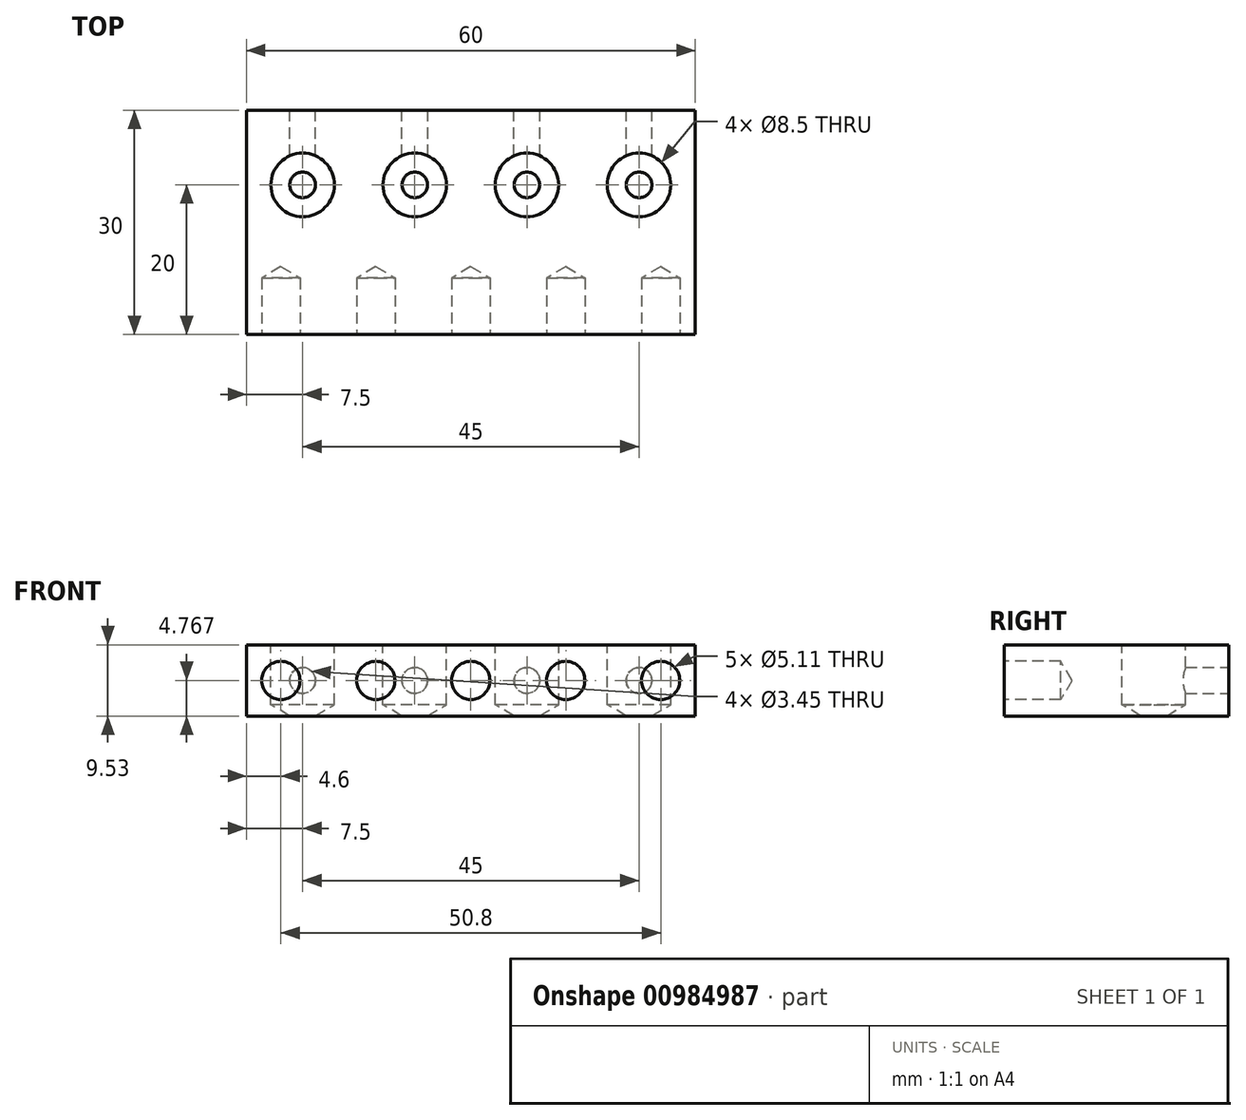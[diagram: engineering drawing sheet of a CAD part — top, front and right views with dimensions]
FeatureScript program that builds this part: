
annotation { "Feature Type Name" : "Feature", "Feature Type Description" : "" }
export const myFeature = defineFeature(function(context is Context, id is Id, definition is map)
    precondition{}
    {
        {
            var Q0;
            Q0=qCreatedBy(makeId("Top.planeOp"),FACE);
            var sketch = newSketch(context, id + "F0", { "sketchPlane" : qUnion([Q0])});
            skLineSegment(sketch, "E0.bottom", {"start": v(0, 0) * mm, "end": v(30, 0) * mm});
            skLineSegment(sketch, "E0.top", {"start": v(0, 30) * mm, "end": v(30, 30) * mm});
            skLineSegment(sketch, "E0.right", {"start": v(30, 0) * mm, "end": v(30, 30) * mm});
            skPoint(sketch, "E1", {"position": v(7.5, 20) * mm});
            skPoint(sketch, "E2.1.0.0", {"position": v(22.5, 20) * mm});
            skLineSegment(sketch, "E2.direction1", {"start": v(7.5, 20) * mm, "end": v(22.5, 20) * mm, "construction": true});
            skLineSegment(sketch, "E3.MirrorCS", {"start": v(0, 0) * mm, "end": v(-30, 0) * mm});
            skPoint(sketch, "E4.MirrorP", {"position": v(-22.5, 20) * mm});
            skLineSegment(sketch, "E5.MirrorCS", {"start": v(-7.5, 20) * mm, "end": v(-22.5, 20) * mm, "construction": true});
            skLineSegment(sketch, "E6.MirrorCS", {"start": v(0, 30) * mm, "end": v(-30, 30) * mm});
            skPoint(sketch, "E7.MirrorP", {"position": v(-7.5, 20) * mm});
            skLineSegment(sketch, "E8.MirrorCS", {"start": v(-30, 0) * mm, "end": v(-30, 30) * mm});
            skSolve(sketch);
        }
        {
            var Q0;
            Q0 = qSketchRegion(id + "F0", true);
            extrude(context, id + "F1", {"entities" : qUnion([Q0]), "oppositeDirection" : true, "depth" : 9.53 * mm, "offsetDistance" : 25 * mm});
        }
        {
            var Q0;
            Q0=sQuery(id+"F0.wireOp",VERTEX,"E4.MirrorP");
            var Q1;
            Q1=sQuery(id+"F0.wireOp",VERTEX,"E7.MirrorP");
            var Q2;
            Q2=sQuery(id+"F0.wireOp",VERTEX,"E1");
            var Q3;
            Q3=sQuery(id+"F0.wireOp",VERTEX,"E2.1.0.0");
            var Q4;
            Q4=makeQuery(id+"F1.opExtrude","SWEPT_BODY",BODY,{"disambiguationData":[OSD([sQuery(id+"F0.wireOp",EDGE,"E0.bottom"),sQuery(id+"F0.wireOp",EDGE,"E0.top"),sQuery(id+"F0.wireOp",EDGE,"E0.right"),sQuery(id+"F0.wireOp",EDGE,"E3.MirrorCS"),sQuery(id+"F0.wireOp",EDGE,"E6.MirrorCS"),sQuery(id+"F0.wireOp",EDGE,"E8.MirrorCS")])]});
            hole(context, id + "F2", {"style" : HoleStyle.SIMPLE, "endStyle" : HoleEndStyle.BLIND, "standardTappedOrClearance" : lookupTablePath({ "standard" : "ISO", "engagement" : "75%", "pitch" : "1.5 mm", "size" : "M10", "type" : "Tapped" }), "standardBlindInLast" : lookupTablePath({ "standard" : "ISO", "fit" : "Normal", "engagement" : "75%", "pitch" : "1.5 mm", "size" : "M10", "type" : "Clearance & tapped" }), "holeDiameter" : 8.5 * mm, "majorDiameter" : 10 * mm, "showTappedDepth" : true, "holeDepth" : 8 * mm, "isTappedThrough" : true, "tappedDepth" : 5 * mm, "tapClearance" : 2, "startFromSketch" : true, "locations" : qUnion([Q0, Q1, Q2, Q3]), "scope" : qUnion([Q4])});
        }
        {
            var Q0;
            Q0=makeQuery(id+"F1.opExtrude","SWEPT_FACE",FACE,{"disambiguationData":[OSD([sQuery(id+"F0.wireOp",EDGE,"E0.bottom"),sQuery(id+"F0.wireOp",EDGE,"E3.MirrorCS")])]});
            var sketch = newSketch(context, id + "F3", { "sketchPlane" : qUnion([Q0])});
            skPoint(sketch, "E9", {"position": v(0, -4.76) * mm});
            skPoint(sketch, "E9.positionSnap0", {"position": v(0, -9.53) * mm});
            skPoint(sketch, "E10.1.0.0", {"position": v(12.7, -4.76) * mm});
            skPoint(sketch, "E10.2.0.0", {"position": v(25.4, -4.76) * mm});
            skLineSegment(sketch, "E10.direction1", {"start": v(0, -4.76) * mm, "end": v(12.7, -4.76) * mm, "construction": true});
            skPoint(sketch, "E11.1.0.0", {"position": v(-12.7, -4.76) * mm});
            skPoint(sketch, "E11.2.0.0", {"position": v(-25.4, -4.76) * mm});
            skLineSegment(sketch, "E11.direction1", {"start": v(0, -4.76) * mm, "end": v(-12.7, -4.76) * mm, "construction": true});
            skSolve(sketch);
        }
        {
            var Q0;
            Q0=sQuery(id+"F3.wireOp",VERTEX,"E11.2.0.0");
            var Q1;
            Q1=sQuery(id+"F3.wireOp",VERTEX,"E11.1.0.0");
            var Q2;
            Q2=sQuery(id+"F3.wireOp",VERTEX,"E9");
            var Q3;
            Q3=sQuery(id+"F3.wireOp",VERTEX,"E10.1.0.0");
            var Q4;
            Q4=sQuery(id+"F3.wireOp",VERTEX,"E10.2.0.0");
            var Q5;
            Q5=makeQuery(id+"F1.opExtrude","SWEPT_BODY",BODY,{"disambiguationData":[OSD([sQuery(id+"F0.wireOp",EDGE,"E0.bottom"),sQuery(id+"F0.wireOp",EDGE,"E0.top"),sQuery(id+"F0.wireOp",EDGE,"E0.right"),sQuery(id+"F0.wireOp",EDGE,"E3.MirrorCS"),sQuery(id+"F0.wireOp",EDGE,"E6.MirrorCS"),sQuery(id+"F0.wireOp",EDGE,"E8.MirrorCS")])]});
            hole(context, id + "F4", {"style" : HoleStyle.SIMPLE, "endStyle" : HoleEndStyle.BLIND, "standardTappedOrClearance" : lookupTablePath({ "standard" : "ANSI", "engagement" : "75%", "pitch" : "20 tpi", "size" : "1/4", "type" : "Tapped" }), "standardBlindInLast" : lookupTablePath({ "standard" : "ANSI", "fit" : "Normal", "engagement" : "75%", "pitch" : "20 tpi", "size" : "1/4", "type" : "Clearance & tapped" }), "holeDiameter" : 5.1 * mm, "majorDiameter" : 6.35 * mm, "showTappedDepth" : true, "holeDepth" : 7.54 * mm, "isTappedThrough" : true, "tappedDepth" : 5 * mm, "tapClearance" : 2, "startFromSketch" : true, "locations" : qUnion([Q0, Q1, Q2, Q3, Q4]), "scope" : qUnion([Q5])});
        }
        {
            var Q0;
            Q0=makeQuery(id+"F1.opExtrude","SWEPT_FACE",FACE,{"disambiguationData":[OSD([sQuery(id+"F0.wireOp",EDGE,"E0.top"),sQuery(id+"F0.wireOp",EDGE,"E6.MirrorCS")])]});
            var sketch = newSketch(context, id + "F5", { "sketchPlane" : qUnion([Q0])});
            skPoint(sketch, "E12", {"position": v(-22.5, -4.76) * mm});
            skPoint(sketch, "E13.1.0.0", {"position": v(-7.5, -4.76) * mm});
            skPoint(sketch, "E13.2.0.0", {"position": v(7.5, -4.76) * mm});
            skPoint(sketch, "E13.3.0.0", {"position": v(22.5, -4.76) * mm});
            skLineSegment(sketch, "E13.direction1", {"start": v(-22.5, -4.76) * mm, "end": v(-7.5, -4.76) * mm, "construction": true});
            skSolve(sketch);
        }
        {
            var Q0;
            Q0=sQuery(id+"F5.wireOp",VERTEX,"E12");
            var Q1;
            Q1=sQuery(id+"F5.wireOp",VERTEX,"E13.1.0.0");
            var Q2;
            Q2=sQuery(id+"F5.wireOp",VERTEX,"E13.2.0.0");
            var Q3;
            Q3=sQuery(id+"F5.wireOp",VERTEX,"E13.3.0.0");
            var Q4;
            Q4=makeQuery(id+"F1.opExtrude","SWEPT_BODY",BODY,{"disambiguationData":[OSD([sQuery(id+"F0.wireOp",EDGE,"E0.bottom"),sQuery(id+"F0.wireOp",EDGE,"E0.top"),sQuery(id+"F0.wireOp",EDGE,"E0.right"),sQuery(id+"F0.wireOp",EDGE,"E3.MirrorCS"),sQuery(id+"F0.wireOp",EDGE,"E6.MirrorCS"),sQuery(id+"F0.wireOp",EDGE,"E8.MirrorCS")])]});
            hole(context, id + "F6", {"style" : HoleStyle.SIMPLE, "endStyle" : HoleEndStyle.BLIND, "standardTappedOrClearance" : lookupTablePath({ "standard" : "ANSI", "engagement" : "75%", "pitch" : "32 tpi", "size" : "#8", "type" : "Tapped" }), "standardBlindInLast" : lookupTablePath({ "standard" : "ANSI", "fit" : "Normal", "engagement" : "75%", "pitch" : "32 tpi", "size" : "#8", "type" : "Clearance & tapped" }), "holeDiameter" : 3.45 * mm, "majorDiameter" : 4.17 * mm, "showTappedDepth" : true, "holeDepth" : 6.6 * mm, "isTappedThrough" : true, "tappedDepth" : 5 * mm, "tapClearance" : 2, "startFromSketch" : true, "locations" : qUnion([Q0, Q1, Q2, Q3]), "scope" : qUnion([Q4])});
        }
    });
